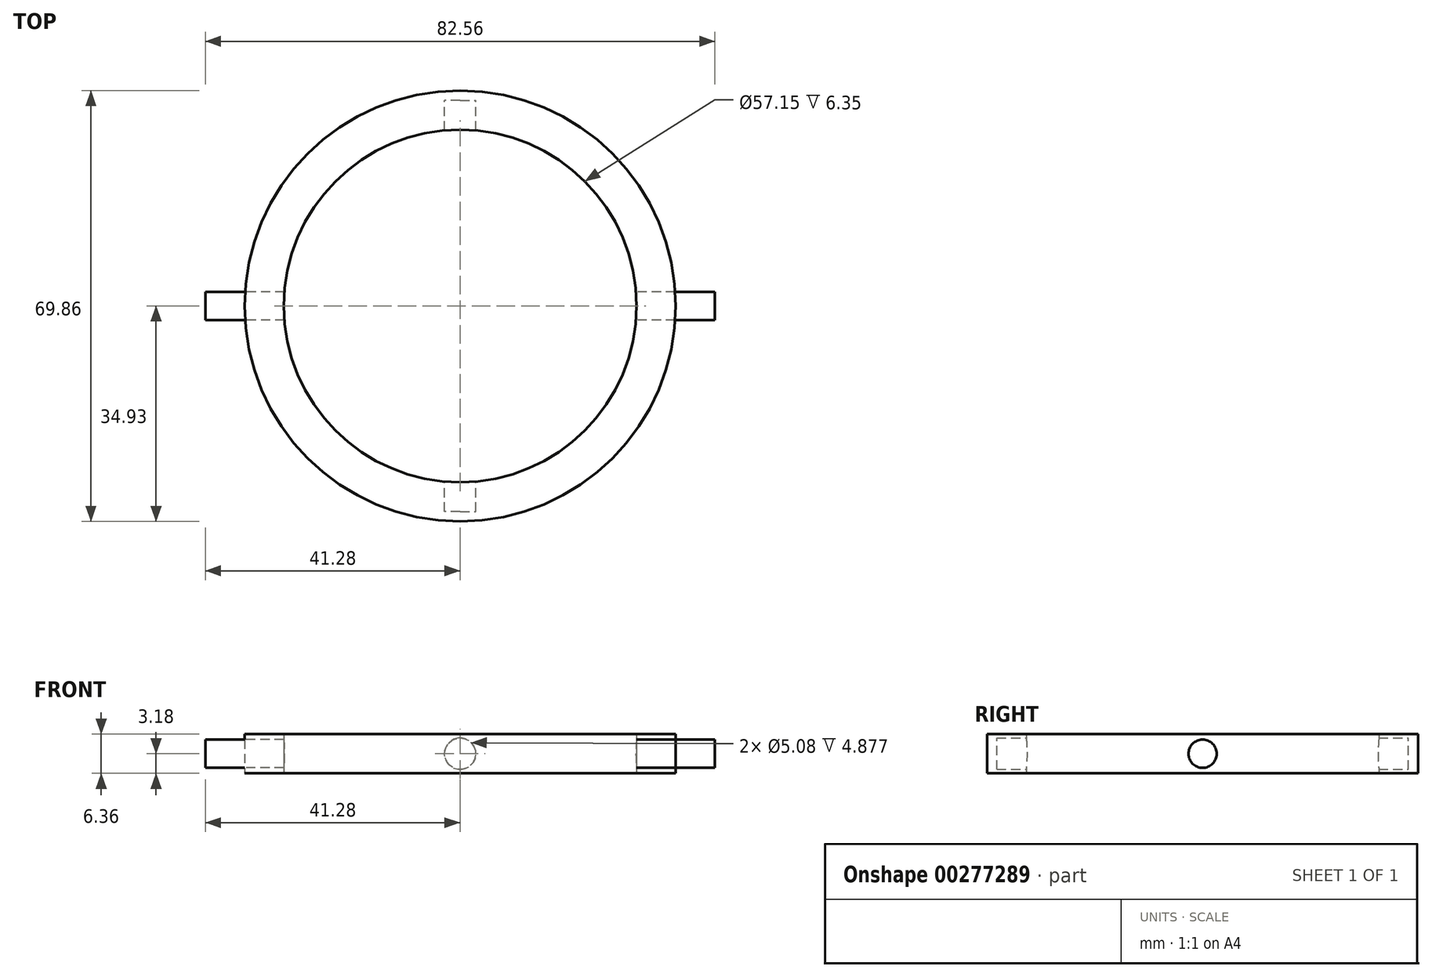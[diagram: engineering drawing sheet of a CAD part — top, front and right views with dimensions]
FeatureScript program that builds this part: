
annotation { "Feature Type Name" : "Feature", "Feature Type Description" : "" }
export const myFeature = defineFeature(function(context is Context, id is Id, definition is map)
    precondition{}
    {
        {
            var Q0;
            Q0=qCreatedBy(makeId("Top.planeOp"),FACE);
            var sketch = newSketch(context, id + "F0", { "sketchPlane" : qUnion([Q0])});
            skCircle(sketch, "E0", {"center": v(0, 0) * mm, "radius": 34.93 * mm});
            skCircle(sketch, "E1.0", {"center": v(0, 0) * mm, "radius": 28.58 * mm});
            skSolve(sketch);
        }
        {
            var Q0;
            Q0 = qSketchRegion(id + "F0", true);
            extrude(context, id + "F1", {"entities" : qUnion([Q0]), "endBound" : BoundingType.SYMMETRIC, "depth" : 6.35 * mm});
        }
        {
            var Q0;
            Q0=qCreatedBy(makeId("Right.planeOp"),FACE);
            var sketch = newSketch(context, id + "F2", { "sketchPlane" : qUnion([Q0])});
            skCircle(sketch, "E2", {"center": v(0, 0) * mm, "radius": 2.29 * mm});
            skSolve(sketch);
        }
        {
            var Q0;
            Q0=makeQuery(id+"F2.imprint","IMPRINT",FACE,{"disambiguationData":[TD([[makeQuery(id+"F2.imprint","IMPRINT",EDGE,{"derivedFrom":sQuery(id+"F2.wireOp",EDGE,"E2")}),1.0]])]});
            extrude(context, id + "F3", {"entities" : qUnion([Q0]), "endBound" : BoundingType.SYMMETRIC, "depth" : 82.55 * mm});
        }
        {
            var Q0;
            Q0=qCreatedBy(makeId("Front.planeOp"),FACE);
            var sketch = newSketch(context, id + "F4", { "sketchPlane" : qUnion([Q0])});
            skCircle(sketch, "E3", {"center": v(0, 0) * mm, "radius": 2.54 * mm});
            skSolve(sketch);
        }
        {
            var Q0;
            Q0=makeQuery(id+"F4.imprint","IMPRINT",FACE,{"disambiguationData":[TD([[makeQuery(id+"F4.imprint","IMPRINT",EDGE,{"derivedFrom":sQuery(id+"F4.wireOp",EDGE,"E3")}),1.0]])]});
            extrude(context, id + "F5", {"entities" : qUnion([Q0]), "operationType" : NewBodyOperationType.REMOVE, "endBound" : BoundingType.SYMMETRIC, "depth" : 66.67 * mm});
        }
        {
            var Q0;
            Q0=makeQuery(id+"F0.imprint","IMPRINT",FACE,{"disambiguationData":[TD([[makeQuery(id+"F0.imprint","IMPRINT",EDGE,{"derivedFrom":sQuery(id+"F0.wireOp",EDGE,"E1.0")}),1.0]])]});
            extrude(context, id + "F6", {"entities" : qUnion([Q0]), "operationType" : NewBodyOperationType.REMOVE, "endBound" : BoundingType.SYMMETRIC, "depth" : 25.4 * mm});
        }
    });
